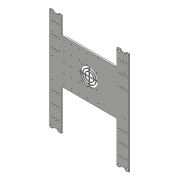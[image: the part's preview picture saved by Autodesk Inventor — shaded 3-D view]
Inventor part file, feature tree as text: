
AUTODESK INVENTOR PART (.ipt)
format: ipt  version: 2018 (Build 220112000, 112)  size: 617,472 bytes
history: native  units: mm
features: sketch x14, extrude x8, hole x6, fillet x6, mirror x5, projected_geometry x5, pattern_linear x2, chamfer x1
ambient origin geometry x8: Origin, YZ Plane, XZ Plane, XY Plane, X Axis, Y Axis, Z Axis, Center Point
bodies: Solid1 (feature_tree)
feature tree (47):
  extrude  "Extrusion1"  Depth=222.8mm
  hole  "Hole1"  [1 undecoded]
  mirror  "Mirror1"
  extrude  "Extrusion2"  Depth=64.56875mm
  extrude  "Extrusion3"  Depth=2.0mm
  mirror  "Mirror2"
  extrude  "Extrusion6"  Depth=6.1mm
  fillet  "Fillet1"  Radius=6.0mm
  hole  "Hole2"  [1 undecoded]
  pattern_linear  "Rectangular Pattern1"  Count1=2 Spacing1=7.0mm
  mirror  "Mirror4"
  mirror  "Mirror5"
  extrude  "Extrusion4"  Depth=1.5mm TaperAngle=0.0deg
  chamfer  "Chamfer1"  Distance=1.5mm Angle=45.0deg
  fillet  "Fillet2"  Radius=3.0mm
  hole  "Hole3"  [1 undecoded]
  hole  "Hole4"  [1 undecoded]
  pattern_linear  "Rectangular Pattern2"  Spacing1=8.0mm  [1 undecoded]
  hole  "Hole5"  [1 undecoded]
  mirror  "Mirror6"
  fillet  "Fillet3"  Radius=16.666667mm
  hole  "Hole6"  [1 undecoded]
  extrude  "Extrusion7"  Depth=1.0mm
  fillet  "Fillet4"  Radius=6.0mm
  fillet  "Fillet5"  Radius=50.0mm
  extrude  "Extrusion8"  Depth=1.0mm
  fillet  "Fillet6"  Radius=90.0mm
  extrude  "Extrusion9"  Depth=1.0mm
  sketch  "Sketch1"  dims[d0=172.0mm d1=222.8mm]
  sketch  "Sketch2"  dims[d2=2.0mm d3=0.0mm d4=214.7248mm]
  sketch  "Sketch3"  dims[d5=17.4625mm d6=64.56875mm]
  sketch  "Sketch4"  dims[d7=5.3mm d8=6.0mm d9=10.4mm d10=2.0mm d11=90.0deg d12=8.0mm d13=20.594885mm d14=5.1mm]
  sketch  "Sketch5"  dims[d15=5.1mm d16=6.1mm d17=6.0mm]
  sketch  "Sketch6"  dims[d18=2.0mm d19=0.0mm d20=120.0mm]
  sketch  "Sketch7"  dims[d21=88.8mm]
  projected_geometry  "Projected Loop1"
  sketch  "Sketch9"  dims[d22=2.0mm d23=0.0mm]
  sketch  "Sketch10"  dims[d24=1.0mm d25=1.0mm]
  sketch  "Sketch11"  dims[d26=50.8mm]
  sketch  "Sketch12"  dims[d28=12.7mm]
  projected_geometry  "Projected Loop2"
  sketch  "Sketch13"  dims[d29=4.3mm d30=6.0mm d31=9.4mm d32=2.0mm d33=90.0deg d34=8.0mm d35=20.594885mm d36=20.0mm d38=7.0mm]
  projected_geometry  "Projected Loop3"
  sketch  "Sketch14"  dims[d39=20.0mm d41=7.0mm d43=1.5mm d44=0.0mm d45=1.5mm d46=2.0mm d47=45.0deg d48=3.0mm]
  projected_geometry  "Projected Loop4"
  sketch  "Sketch15"  dims[d49=58.0mm d50=86.0mm d51=1.567mm d52=4.0mm d53=4.4mm d54=2.0mm d55=90.0deg d56=6.3mm d57=20.594885mm d58=28.4mm d59=8.0mm d62=50.0mm d63=16.666667mm d64=16.666667mm d65=16.666667mm d66=6.0mm d67=1.567mm d68=4.0mm d69=4.4mm d70=2.0mm d71=90.0deg d72=6.3mm d73=20.594885mm d74=50.0mm d76=21.0mm d77=5.0mm d78=90.0mm d79=5.0mm d80=1.567mm d81=4.0mm d82=4.4mm d83=2.0mm d84=90.0deg d85=6.3mm d86=20.594885mm d87=120.0mm d88=38.0mm d89=10.0mm d90=0.0mm d91=100.0mm d92=25.4mm d93=2.0mm d94=42.0624mm d95=32.0mm d96=32.0mm d97=2.459mm d98=6.0mm d99=6.3mm d100=2.0mm d101=90.0deg d102=8.8mm d103=20.594885mm d104=40.5mm d105=40.5mm d106=2.0mm d107=0.0mm d108=1.0mm d109=0.5mm d110=38.0mm d111=3.0mm d112=0.0mm d113=0.5mm d114=1.0mm d115=40.0mm d116=40.0mm d117=1.0mm d118=20.0mm d119=18.0mm d120=28.0mm d121=30.0mm d122=1.0mm d123=0.0mm]
  projected_geometry  "Projected Loop5"
note: 7 required parameter values undecoded (feature->parameter linkage not recoverable at this tier; creation-order binding heuristic only, values carry confidence <= 0.55)
